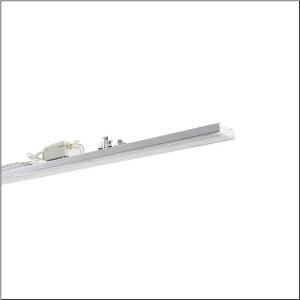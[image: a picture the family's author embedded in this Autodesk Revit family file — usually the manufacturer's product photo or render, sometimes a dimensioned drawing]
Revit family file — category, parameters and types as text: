
# Revit family: licross_r__21_recessed_mo_52te12dn4axg3c_0e6c
name_source: partatom
category: Lighting Fixtures
units: mm (PartAtom-declared; Revit-internal decimal feet)

## family parameters
Cut with Voids When Loaded = No
Host = Face
Light Source = No
Part Type = Normal
Room Calculation Point = No
Round Connector Dimension = Use Diameter
Shared = No

## types (1)
- --- (1 x LED, 950 lm, 6.7 W, 4000K)
    Apparent Load = 7 VA
    CIE Flux Codes = 72 92 99 100 100
    Color Rendering = 80
    Color Temperature = 4000K
    Default Elevation = 1800 mm
    Description = Licross® 21 Recessed MO, luminaire insert, of sheet steel, galvanised, coil coated, white, length: 1.500mm, width: 66mm, height: 67mm, LED rated luminous flux: 10.280lm, light colour: 840, control gear: DALI 2, with plug, 6-pole, with phase selection, for trunking rail, 14-core, mains connection: 220..240V, AC, 50/60Hz, rated input power: 62W, halogen-free wiring, for emergency light function, for trunking rail, 14-core, converter,control gear: single battery element, battery: LiFeP04, 9Ah, primary optical cover: cover, of PMMA, light emission: direct distribution, primary light characteristic: symmetric, protection rating (complete): IP54, insulation class (complete): insulation class I (protective earthing), certification: CE, UKCA, protection symbol: D if used in an environment with non-conductive dust loads with corresponding accessories, impact resistance: IK06, permissible ambient temperature for indoor applications: +5..+35°C, standard: EN 60598-2-22, LABS conformity tested according to VDMA 24364:2018-05, reducing of maximum allowable ambient temperature of 5°C with ceiling mounting, corresponds to IFS (International Featured Standards) requirements for safety and quality in the food industry, packaging unit: 1 piece
    Height = 58 mm
    Lamp = 1 x LED
    Lamp Light Flux = 950 lm
    Lamp Power = 6.7 W
    Lamp count = 1
    Length = 1500 mm
    Luminous efficacy = 142 lm/W
    Manufacturer = Siteco
    ModVariant = No
    Model = 52TE12DN4AXG3C
    Mounting Place = Ceiling
    Mounting Type = Pendant
    Number of Poles = 1
    OnlyDefault = Yes
    Power Factor = 1
    Product Name = Licross® 21 Recessed MO
    Product group = luminaire insert
    ProductGroupID = 901
    Protection Class = Protection class I
    Protection Degree = IP 54
    RLX_Detail_Level = 1
    RLX_Emergency_Light_Flux = 0 lm
    RLX_Emergency_Type = 0
    RLX_Emergency_Type_DB = No
    RlxData = <blob elided: 25005 chars, md5=d9ab2a3f>
    Socket = socket
    Standby Power = 0 W
    System Light Flux = 950 lm
    System Power = 7 W
    Type Comments = : emergency light operation: 3 h
    Type Image = l_1296930.jpg
    URL = http://relux.com
    VarID = @adj_040181
    Voltage = 0 V
    Weight = 0.00 kg
    Width = 66 mm

## geometry (parser evidence)
native form markers: Blend x4, Sweep x9
no freeform markers — native parametric forms only
